# Revit family: Diffuser-Carnes-SPAB-Round_Neck
name_source: partatom
category: Duct Accessories
revit_build: Autodesk Revit Architecture 2013 (Build: 20120221_2030(x64)
units: mm (PartAtom-declared; Revit-internal decimal feet)

## types (13) — shared parameters
Catalog = http://www.carnes.com
Default Elevation = 0"
Description = Perforated Diffusers
Diameter = 5"
Diffuser Plate = Metal - Carnes - Plate - Mesh
Flow = 0 CFM
Height C = 2 3/4"
Inlet Diameter D = 5"
Inner Width = 4 15/16"
Manufacturer = CARNES COMPANY
Model = SPAB
Panel Options = http://www.carnes.com
Product Page URL = http://www.carnes.com
Radius = 3"
Specification Sheet = http://www.carnes.com
Subcatagory = Air Distribution
Supply Connection = Diffuser Supply Connector
Supply Connector = No
URL = http://www.carnes.com
Unit = Metal - Carnes - Steel Galvanized

## per-type parameters (varying)
| type | Depth B | Width A |
| SPAB 12x5 | 12" | 12" |
| SPAB 12x6 | 12" | 12" |
| SPAB 12x7 | 12" | 12" |
| SPAB 12x8 | 12" | 12" |
| SPAB 24x5 | 24" | 24" |
| SPAB 24x6 | 24" | 24" |
| SPAB 24x7 | 24" | 24" |
| SPAB 24x8 | 24" | 24" |
| SPAB 24x10 | 24" | 24" |
| SPAB 24x12 | 24" | 24" |
| SPAB 24x14 | 24" | 24" |
| SPAB 24x16 | 24" | 24" |
| SPAB 24x18 | 24" | 24" |

## geometry (parser evidence)
native form markers: Blend x2, Sweep x8
no freeform markers — native parametric forms only
